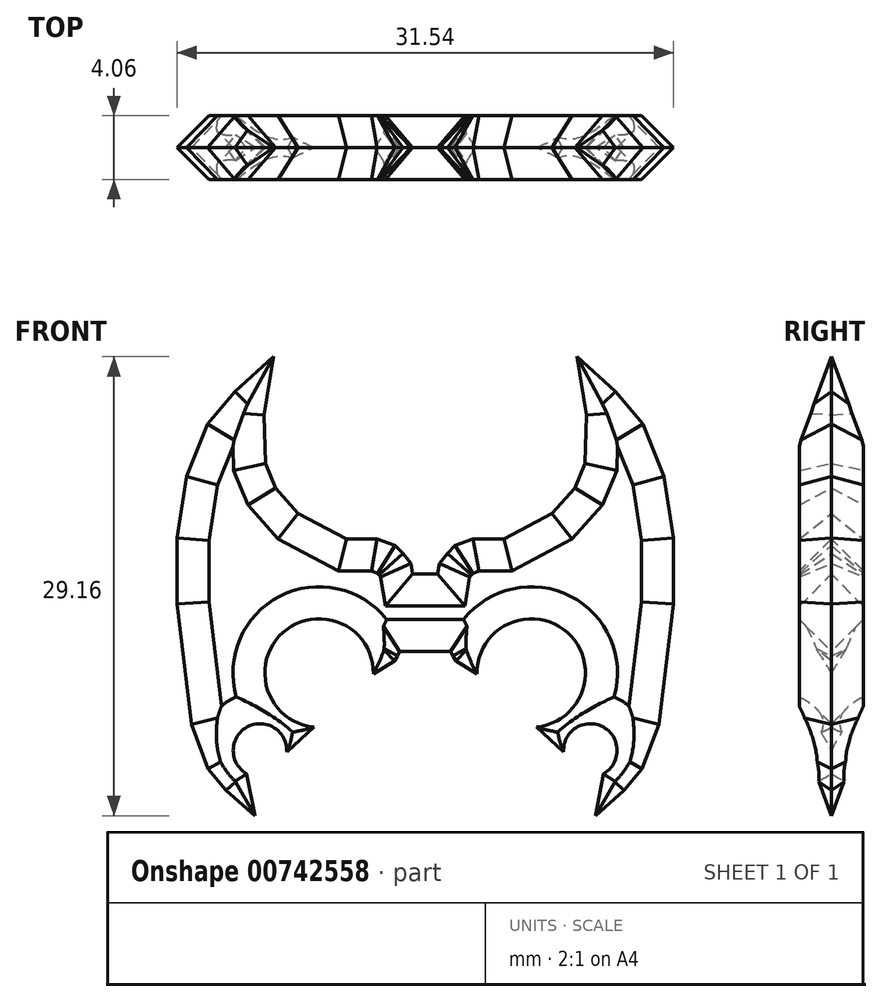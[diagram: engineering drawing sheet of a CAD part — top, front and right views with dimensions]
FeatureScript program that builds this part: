
annotation { "Feature Type Name" : "Feature", "Feature Type Description" : "" }
export const myFeature = defineFeature(function(context is Context, id is Id, definition is map)
    precondition{}
    {
        {
            var Q0;
            Q0=qCreatedBy(makeId("Front.planeOp"),FACE);
            var sketch = newSketch(context, id + "F0", { "sketchPlane" : qUnion([Q0])});
            skLineSegment(sketch, "E0", {"start": v(2.5, 1.63) * mm, "end": v(4.03, 2.44) * mm});
            skLineSegment(sketch, "E1", {"start": v(4.03, 2.44) * mm, "end": v(4.76, 3.26) * mm});
            skLineSegment(sketch, "E2", {"start": v(4.76, 3.26) * mm, "end": v(5.08, 4.03) * mm});
            skLineSegment(sketch, "E3", {"start": v(5.08, 4.03) * mm, "end": v(5.12, 5.58) * mm});
            skLineSegment(sketch, "E4", {"start": v(5.12, 5.58) * mm, "end": v(4.81, 7.42) * mm});
            skLineSegment(sketch, "E5", {"start": v(4.81, 7.42) * mm, "end": v(6.04, 6.31) * mm});
            skLineSegment(sketch, "E6", {"start": v(6.04, 6.31) * mm, "end": v(6.92, 5.28) * mm});
            skLineSegment(sketch, "E7", {"start": v(6.92, 5.28) * mm, "end": v(7.58, 3.62) * mm});
            skLineSegment(sketch, "E8", {"start": v(7.58, 3.62) * mm, "end": v(7.89, 1.67) * mm});
            skLineSegment(sketch, "E9", {"start": v(7.89, 1.67) * mm, "end": v(7.89, -0.43) * mm});
            skLineSegment(sketch, "E10", {"start": v(7.89, -0.43) * mm, "end": v(7.43, -4.26) * mm});
            skLineSegment(sketch, "E11", {"start": v(7.43, -4.26) * mm, "end": v(6.9, -5.67) * mm});
            skLineSegment(sketch, "E12", {"start": v(6.9, -5.67) * mm, "end": v(6.32, -6.36) * mm});
            skLineSegment(sketch, "E13", {"start": v(6.32, -6.36) * mm, "end": v(5.4, -7.16) * mm});
            skLineSegment(sketch, "E14", {"start": v(5.4, -7.16) * mm, "end": v(5.67, -5.82) * mm});
            skArc(sketch, "E15", {"start": v(5.67, -5.82) * mm, "mid": v(5.65, -4.34) * mm, "end": v(4.4, -5.12) * mm});
            skLineSegment(sketch, "E16", {"start": v(0.98, -2.23) * mm, "end": v(1.64, -2.65) * mm});
            skLineSegment(sketch, "E17", {"start": v(3.54, -4.34) * mm, "end": v(4.4, -5.12) * mm});
            skLineSegment(sketch, "E18", {"start": v(2.5, 1.63) * mm, "end": v(1.52, 1.63) * mm});
            skLineSegment(sketch, "E19", {"start": v(1.52, 1.63) * mm, "end": v(0.95, 1.42) * mm});
            skLineSegment(sketch, "E20", {"start": v(0.95, 1.42) * mm, "end": v(0.7, 1.17) * mm});
            skArc(sketch, "E21", {"start": v(3.54, -4.34) * mm, "mid": v(4.52, -1.34) * mm, "end": v(1.64, -2.65) * mm});
            skLineSegment(sketch, "E22", {"start": v(0.7, 1.17) * mm, "end": v(0.45, 0.85) * mm});
            skLineSegment(sketch, "E23", {"start": v(0.45, 0.85) * mm, "end": v(0.4, 0.51) * mm});
            skLineSegment(sketch, "E24", {"start": v(0.4, 0.51) * mm, "end": v(0, 0.51) * mm});
            skLineSegment(sketch, "E25", {"start": v(0.98, -2.23) * mm, "end": v(0.88, -2.09) * mm});
            skLineSegment(sketch, "E26", {"start": v(0.88, -2.09) * mm, "end": v(0.81, -1.94) * mm});
            skLineSegment(sketch, "E27", {"start": v(0.81, -1.94) * mm, "end": v(0, -1.94) * mm});
            skLineSegment(sketch, "E28.MirrorCS", {"start": v(-6.9, -5.67) * mm, "end": v(-6.32, -6.36) * mm});
            skLineSegment(sketch, "E29.MirrorCS", {"start": v(-0.98, -2.23) * mm, "end": v(-0.88, -2.09) * mm});
            skLineSegment(sketch, "E30.MirrorCS", {"start": v(-0.4, 0.51) * mm, "end": v(0, 0.51) * mm});
            skLineSegment(sketch, "E31.MirrorCS", {"start": v(-0.81, -1.94) * mm, "end": v(0, -1.94) * mm});
            skLineSegment(sketch, "E32.MirrorCS", {"start": v(-4.76, 3.26) * mm, "end": v(-5.08, 4.03) * mm});
            skLineSegment(sketch, "E33.MirrorCS", {"start": v(-0.95, 1.42) * mm, "end": v(-0.7, 1.17) * mm});
            skLineSegment(sketch, "E34.MirrorCS", {"start": v(-3.54, -4.34) * mm, "end": v(-4.4, -5.12) * mm});
            skLineSegment(sketch, "E35.MirrorCS", {"start": v(-0.7, 1.17) * mm, "end": v(-0.45, 0.85) * mm});
            skLineSegment(sketch, "E36.MirrorCS", {"start": v(-0.88, -2.09) * mm, "end": v(-0.81, -1.94) * mm});
            skLineSegment(sketch, "E37.MirrorCS", {"start": v(-1.52, 1.63) * mm, "end": v(-0.95, 1.42) * mm});
            skLineSegment(sketch, "E38.MirrorCS", {"start": v(-0.45, 0.85) * mm, "end": v(-0.4, 0.51) * mm});
            skLineSegment(sketch, "E39.MirrorCS", {"start": v(-6.32, -6.36) * mm, "end": v(-5.4, -7.16) * mm});
            skLineSegment(sketch, "E40.MirrorCS", {"start": v(-0.98, -2.23) * mm, "end": v(-1.64, -2.65) * mm});
            skLineSegment(sketch, "E41.MirrorCS", {"start": v(-4.03, 2.44) * mm, "end": v(-4.76, 3.26) * mm});
            skLineSegment(sketch, "E42.MirrorCS", {"start": v(-7.89, -0.43) * mm, "end": v(-7.43, -4.26) * mm});
            skLineSegment(sketch, "E43.MirrorCS", {"start": v(-6.04, 6.31) * mm, "end": v(-6.92, 5.28) * mm});
            skLineSegment(sketch, "E44.MirrorCS", {"start": v(-7.43, -4.26) * mm, "end": v(-6.9, -5.67) * mm});
            skLineSegment(sketch, "E45.MirrorCS", {"start": v(-2.5, 1.63) * mm, "end": v(-4.03, 2.44) * mm});
            skArc(sketch, "E46.MirrorCS", {"start": v(-5.67, -5.82) * mm, "mid": v(-5.65, -4.34) * mm, "end": v(-4.4, -5.12) * mm});
            skLineSegment(sketch, "E47.MirrorCS", {"start": v(-7.58, 3.62) * mm, "end": v(-7.89, 1.67) * mm});
            skLineSegment(sketch, "E48.MirrorCS", {"start": v(-2.5, 1.63) * mm, "end": v(-1.52, 1.63) * mm});
            skLineSegment(sketch, "E49.MirrorCS", {"start": v(-5.12, 5.58) * mm, "end": v(-4.81, 7.42) * mm});
            skLineSegment(sketch, "E50.MirrorCS", {"start": v(-5.08, 4.03) * mm, "end": v(-5.12, 5.58) * mm});
            skLineSegment(sketch, "E51.MirrorCS", {"start": v(-7.89, 1.67) * mm, "end": v(-7.89, -0.43) * mm});
            skLineSegment(sketch, "E52.MirrorCS", {"start": v(-5.4, -7.16) * mm, "end": v(-5.67, -5.82) * mm});
            skArc(sketch, "E53.MirrorCS", {"start": v(-3.54, -4.34) * mm, "mid": v(-4.52, -1.34) * mm, "end": v(-1.64, -2.65) * mm});
            skLineSegment(sketch, "E54.MirrorCS", {"start": v(-6.92, 5.28) * mm, "end": v(-7.58, 3.62) * mm});
            skLineSegment(sketch, "E55.MirrorCS", {"start": v(-4.81, 7.42) * mm, "end": v(-6.04, 6.31) * mm});
            skSolve(sketch);
        }
        {
            var Q0;
            Q0=makeQuery(id+"F0.imprint","IMPRINT",FACE,{"disambiguationData":[TD([[makeQuery(id+"F0.imprint","IMPRINT",EDGE,{"derivedFrom":sQuery(id+"F0.wireOp",EDGE,"E0")}),-1.0]])]});
            extrude(context, id + "F1", {"entities" : qUnion([Q0]), "endBound" : BoundingType.SYMMETRIC, "depth" : 2.03 * mm, "offsetDistance" : 25.4 * mm, "hasDraft" : true, "draftAngle" : 45 * degree, "draftPullDirection" : true});
        }
        {
            var Q0;
            Q0=makeQuery(id+"F1.*.split.splitOp","SPLIT",BODY,{"derivedFrom":makeQuery(id+"F1.opExtrude","SWEPT_BODY",BODY,{"disambiguationData":[OSD([sQuery(id+"F0.wireOp",EDGE,"E0"),sQuery(id+"F0.wireOp",EDGE,"E1"),sQuery(id+"F0.wireOp",EDGE,"E2"),sQuery(id+"F0.wireOp",EDGE,"E3"),sQuery(id+"F0.wireOp",EDGE,"E4"),sQuery(id+"F0.wireOp",EDGE,"E5"),sQuery(id+"F0.wireOp",EDGE,"E6"),sQuery(id+"F0.wireOp",EDGE,"E7"),sQuery(id+"F0.wireOp",EDGE,"E8"),sQuery(id+"F0.wireOp",EDGE,"E9"),sQuery(id+"F0.wireOp",EDGE,"E10"),sQuery(id+"F0.wireOp",EDGE,"E11"),sQuery(id+"F0.wireOp",EDGE,"E12"),sQuery(id+"F0.wireOp",EDGE,"E13"),sQuery(id+"F0.wireOp",EDGE,"E14"),sQuery(id+"F0.wireOp",EDGE,"E15"),sQuery(id+"F0.wireOp",EDGE,"E16"),sQuery(id+"F0.wireOp",EDGE,"E17"),sQuery(id+"F0.wireOp",EDGE,"E18"),sQuery(id+"F0.wireOp",EDGE,"E19"),sQuery(id+"F0.wireOp",EDGE,"E20"),sQuery(id+"F0.wireOp",EDGE,"E21"),sQuery(id+"F0.wireOp",EDGE,"E22"),sQuery(id+"F0.wireOp",EDGE,"E23"),sQuery(id+"F0.wireOp",EDGE,"E24"),sQuery(id+"F0.wireOp",EDGE,"E25"),sQuery(id+"F0.wireOp",EDGE,"E26"),sQuery(id+"F0.wireOp",EDGE,"E27"),sQuery(id+"F0.wireOp",EDGE,"E28.MirrorCS"),sQuery(id+"F0.wireOp",EDGE,"E29.MirrorCS"),sQuery(id+"F0.wireOp",EDGE,"E30.MirrorCS"),sQuery(id+"F0.wireOp",EDGE,"E31.MirrorCS"),sQuery(id+"F0.wireOp",EDGE,"E32.MirrorCS"),sQuery(id+"F0.wireOp",EDGE,"E33.MirrorCS"),sQuery(id+"F0.wireOp",EDGE,"E34.MirrorCS"),sQuery(id+"F0.wireOp",EDGE,"E35.MirrorCS"),sQuery(id+"F0.wireOp",EDGE,"E36.MirrorCS"),sQuery(id+"F0.wireOp",EDGE,"E37.MirrorCS"),sQuery(id+"F0.wireOp",EDGE,"E38.MirrorCS"),sQuery(id+"F0.wireOp",EDGE,"E39.MirrorCS"),sQuery(id+"F0.wireOp",EDGE,"E40.MirrorCS"),sQuery(id+"F0.wireOp",EDGE,"E41.MirrorCS"),sQuery(id+"F0.wireOp",EDGE,"E42.MirrorCS"),sQuery(id+"F0.wireOp",EDGE,"E43.MirrorCS"),sQuery(id+"F0.wireOp",EDGE,"E44.MirrorCS"),sQuery(id+"F0.wireOp",EDGE,"E45.MirrorCS"),sQuery(id+"F0.wireOp",EDGE,"E46.MirrorCS"),sQuery(id+"F0.wireOp",EDGE,"E47.MirrorCS"),sQuery(id+"F0.wireOp",EDGE,"E48.MirrorCS"),sQuery(id+"F0.wireOp",EDGE,"E49.MirrorCS"),sQuery(id+"F0.wireOp",EDGE,"E50.MirrorCS"),sQuery(id+"F0.wireOp",EDGE,"E51.MirrorCS"),sQuery(id+"F0.wireOp",EDGE,"E52.MirrorCS"),sQuery(id+"F0.wireOp",EDGE,"E53.MirrorCS"),sQuery(id+"F0.wireOp",EDGE,"E54.MirrorCS"),sQuery(id+"F0.wireOp",EDGE,"E55.MirrorCS")])]})});
            var Q1;
            Q1=qCreatedBy(makeId("Origin.pointOp"),VERTEX);
            transform(context, id + "F2", {"entities" : qUnion([Q0]), "transformType" : TransformType.SCALE_UNIFORMLY, "scale" : 2, "scalePoint" : qUnion([Q1]), "makeCopy" : false});
        }
    });
